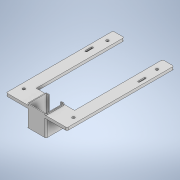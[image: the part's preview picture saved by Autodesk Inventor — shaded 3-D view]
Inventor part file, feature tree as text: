
AUTODESK INVENTOR PART (.ipt)
format: ipt  version: 2020 (Build 240168000, 168)  size: 289,792 bytes
history: native  units: in
note: dims shown in document units (in); Inventor stores cm internally (conversion verified against a paired STEP export)
features: extrude x7, sketch x7, fillet x3, plane x2, mirror x2, hole x1
ambient origin geometry x8: Origin, YZ Plane, XZ Plane, XY Plane, X Axis, Y Axis, Z Axis, Center Point
bodies: Solid1 (feature_tree)
feature tree (22):
  extrude  "Extrusion1"  Depth=1.8504in
  extrude  "Extrusion2"  Depth=1.9685in TaperAngle=0.0deg
  extrude  "Extrusion5"  Depth=2.0669in TaperAngle=0.0deg
  extrude  "Extrusion6"  Depth=8.6614in TaperAngle=0.0deg
  hole  "Hole1"  [1 undecoded]
  extrude  "Extrusion7"  Depth=0.3346in
  extrude  "Extrusion8"  Depth=0.1575in TaperAngle=0.0deg
  extrude  "Extrusion9"  Depth=0.1772in
  plane  "Work Plane2"
  mirror  "Mirror4"
  fillet  "Fillet5"  Radius=0.3937in
  fillet  "Fillet6"  Radius=0.1772in
  fillet  "Fillet7"  Radius=0.5906in
  plane  "Work Plane3"
  mirror  "Mirror5"
  sketch  "Sketch1"  dims[d0=1.8504in d1=1.8504in]
  sketch  "Sketch6"  dims[d2=2.0472in d3=0.0in d7=1.9685in d8=0.0in]
  sketch  "Sketch7"  dims[d26=0.2756in d27=2.0669in d28=0.0in]
  sketch  "Sketch8"  dims[d29=1.1024in d30=8.6614in d31=0.0in]
  sketch  "Sketch9"  dims[d36=0.1575in d37=0.2362in d38=0.2559in d39=0.1575in d40=90.0deg d41=0.315in d42=0.8108in d43=0.3346in]
  sketch  "Sketch10"  dims[d44=0.3937in d46=0.3346in]
  sketch  "Sketch11"  dims[d47=0.5906in d48=0.1575in d49=0.0in d50=0.1772in d51=0.3937in d53=0.1772in d54=0.5906in d55=0.1575in d56=0.0in d62=1.6929in d63=1.6929in d64=1.8504in d65=0.2559in d66=0.2559in d67=1.1811in d68=0.0787in d69=0.0in d71=0.1181in d72=0.1181in d73=0.1181in d74=0.1181in d76=2.4409in d77=2.4409in d78=1.1811in d75=0.0197in d79=0.0344in d80=0.0344in]
note: 1 required parameter value undecoded (feature->parameter linkage not recoverable at this tier; creation-order binding heuristic only, values carry confidence <= 0.55)
